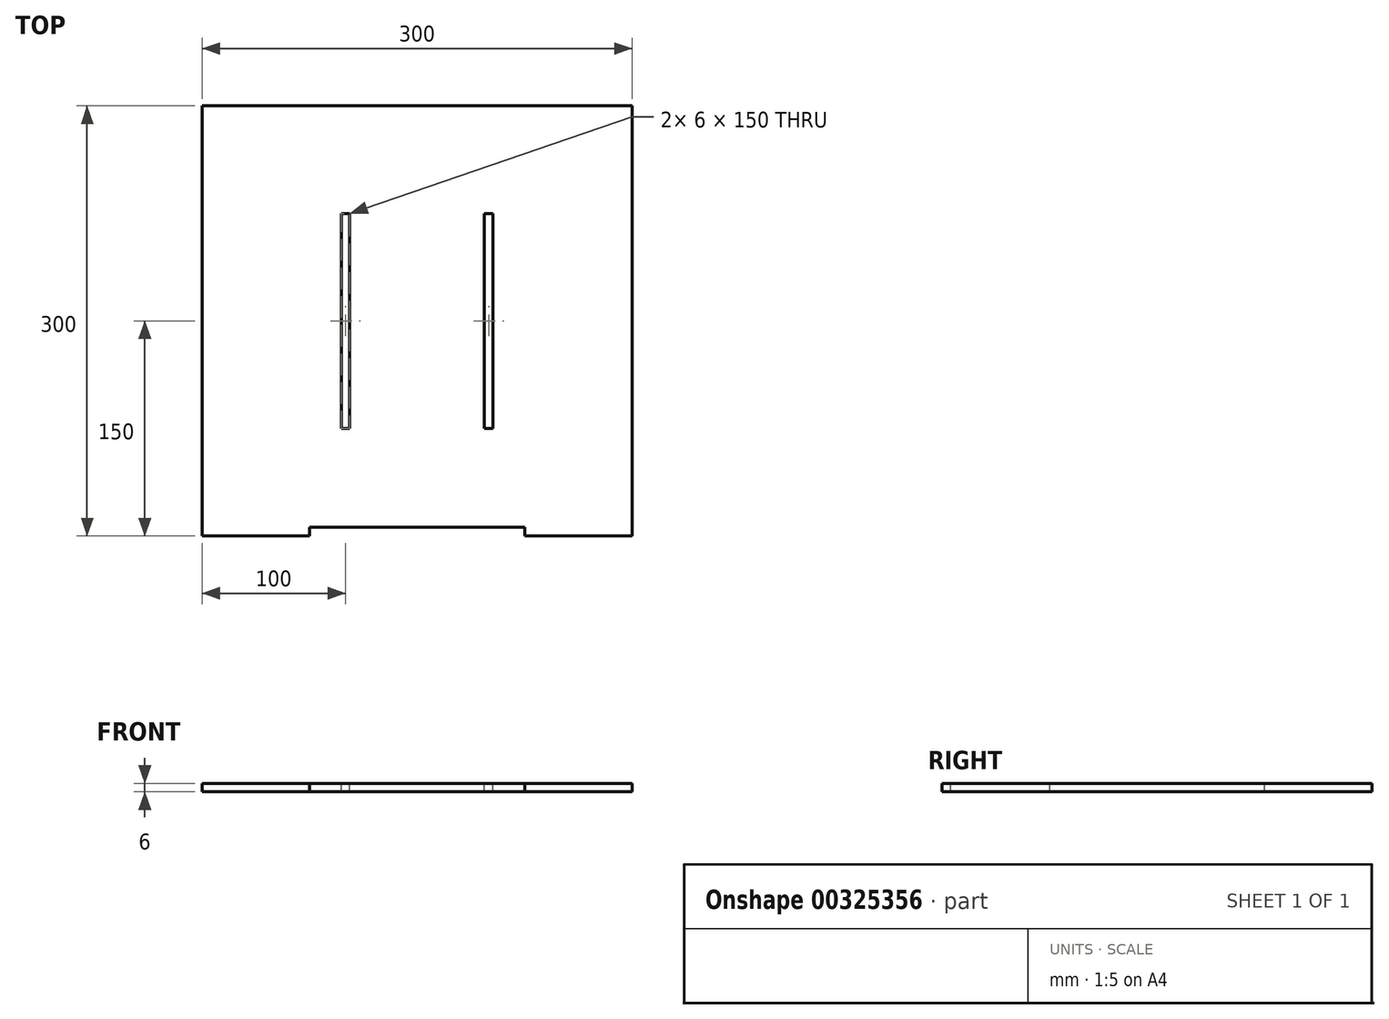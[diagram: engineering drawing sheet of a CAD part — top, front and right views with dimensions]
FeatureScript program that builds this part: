
annotation { "Feature Type Name" : "Feature", "Feature Type Description" : "" }
export const myFeature = defineFeature(function(context is Context, id is Id, definition is map)
    precondition{}
    {
        {
            var Q0;
            Q0=qCreatedBy(makeId("Top.planeOp"),FACE);
            var sketch = newSketch(context, id + "F0", { "sketchPlane" : qUnion([Q0])});
            skLineSegment(sketch, "E0.bottom", {"start": v(-150, 150) * mm, "end": v(150, 150) * mm});
            skLineSegment(sketch, "E0.top", {"start": v(-150, -150) * mm, "end": v(150, -150) * mm});
            skLineSegment(sketch, "E0.left", {"start": v(-150, 150) * mm, "end": v(-150, -150) * mm});
            skLineSegment(sketch, "E0.right", {"start": v(150, 150) * mm, "end": v(150, -150) * mm});
            skPoint(sketch, "E0.middle", {"position": v(0, 0) * mm});
            skSolve(sketch);
        }
        {
            var Q0;
            Q0=makeQuery(id+"F0.imprint","IMPRINT",FACE,{"disambiguationData":[TD([[makeQuery(id+"F0.imprint","IMPRINT",EDGE,{"derivedFrom":sQuery(id+"F0.wireOp",EDGE,"E0.bottom")}),-1.0]])]});
            extrude(context, id + "F1", {"entities" : qUnion([Q0]), "depth" : 6 * mm});
        }
        {
            var Q0;
            Q0=makeQuery(id+"F1.opExtrude","CAP_FACE",FACE,{"disambiguationData":[OSD([sQuery(id+"F0.wireOp",EDGE,"E0.bottom"),sQuery(id+"F0.wireOp",EDGE,"E0.top"),sQuery(id+"F0.wireOp",EDGE,"E0.left"),sQuery(id+"F0.wireOp",EDGE,"E0.right")])],"isStart":false});
            var sketch = newSketch(context, id + "F2", { "sketchPlane" : qUnion([Q0])});
            skLineSegment(sketch, "E1", {"start": v(0, 150) * mm, "end": v(0, -150) * mm, "construction": true});
            skLineSegment(sketch, "E2.bottom", {"start": v(-75, -150) * mm, "end": v(75, -150) * mm});
            skLineSegment(sketch, "E2.top", {"start": v(-75, -144) * mm, "end": v(75, -144) * mm});
            skLineSegment(sketch, "E2.left", {"start": v(-75, -150) * mm, "end": v(-75, -144) * mm});
            skLineSegment(sketch, "E2.right", {"start": v(75, -150) * mm, "end": v(75, -144) * mm});
            skPoint(sketch, "E2.middle", {"position": v(0, -147) * mm});
            skSolve(sketch);
        }
        {
            var Q0;
            Q0=qSketchRegion(id+"F2",true);
            extrude(context, id + "F3", {"entities" : qUnion([Q0]), "operationType" : NewBodyOperationType.REMOVE, "endBound" : BoundingType.UP_TO_NEXT, "oppositeDirection" : true, "depth" : 25 * mm});
        }
        {
            var Q0;
            Q0=qCreatedBy(makeId("Right.planeOp"),FACE);
            var sketch = newSketch(context, id + "F4", { "sketchPlane" : qUnion([Q0])});
            skLineSegment(sketch, "E3", {"start": v(0, 0) * mm, "end": v(0, 53.51) * mm, "construction": true});
            skSolve(sketch);
        }
        {
            var Q0;
            Q0=makeQuery(id+"F1.opExtrude","CAP_FACE",FACE,{"disambiguationData":[OSD([sQuery(id+"F0.wireOp",EDGE,"E0.bottom"),sQuery(id+"F0.wireOp",EDGE,"E0.top"),sQuery(id+"F0.wireOp",EDGE,"E0.left"),sQuery(id+"F0.wireOp",EDGE,"E0.right")])],"isStart":false});
            var sketch = newSketch(context, id + "F5", { "sketchPlane" : qUnion([Q0])});
            skLineSegment(sketch, "E4.bottom", {"start": v(-47, -75) * mm, "end": v(-53, -75) * mm});
            skLineSegment(sketch, "E4.top", {"start": v(-47, 75) * mm, "end": v(-53, 75) * mm});
            skLineSegment(sketch, "E4.left", {"start": v(-47, -75) * mm, "end": v(-47, 75) * mm});
            skLineSegment(sketch, "E4.right", {"start": v(-53, -75) * mm, "end": v(-53, 75) * mm});
            skPoint(sketch, "E4.middle", {"position": v(-50, 0) * mm});
            skLineSegment(sketch, "E5", {"start": v(0, 144) * mm, "end": v(0, -144) * mm});
            skPoint(sketch, "E6.MirrorP", {"position": v(50, 0) * mm});
            skLineSegment(sketch, "E7.MirrorCS", {"start": v(53, -75) * mm, "end": v(53, 75) * mm});
            skLineSegment(sketch, "E8.MirrorCS", {"start": v(47, -75) * mm, "end": v(47, 75) * mm});
            skLineSegment(sketch, "E9.MirrorCS", {"start": v(47, -75) * mm, "end": v(53, -75) * mm});
            skLineSegment(sketch, "E10.MirrorCS", {"start": v(47, 75) * mm, "end": v(53, 75) * mm});
            skSolve(sketch);
        }
        {
            var Q0;
            Q0 = qSketchRegion(id + "F5", true);
            extrude(context, id + "F6", {"entities" : qUnion([Q0]), "operationType" : NewBodyOperationType.REMOVE, "endBound" : BoundingType.UP_TO_NEXT, "oppositeDirection" : true, "depth" : 25 * mm});
        }
    });
